FCSTD DOCUMENT  (FreeCAD 1.0R39109 (Git))
Label: L_Triangla
License: All rights reserved
LicenseURL: https://en.wikipedia.org/wiki/All_rights_reserved
objects: Sketcher::SketchObject×1, PartDesign::Body×1
note: 3 computed .brp shape members not serialized (recipe doc carries the construction recipe); baked Part::Feature solids carry a one-line shape summary decoded from their .brp

FEATURE [Sketcher::SketchObject] Sketch
  ArcFitTolerance = 1e-06
  AttachmentSupport = -> [XY_Plane]
  FullyConstrained = true
  MakeInternals = false
  MapMode = 5
  sketch-geometry (8):
    g0: LineSegment StartX=0 StartY=0 StartZ=0 EndX=45 EndY=77.9423 EndZ=0
    g1: LineSegment StartX=45 StartY=77.9423 StartZ=0 EndX=89.9999 EndY=0 EndZ=0
    g2: LineSegment StartX=89.9999 StartY=0 StartZ=0 EndX=0 EndY=0 EndZ=0
    g3: Circle CenterX=15 CenterY=10 CenterZ=0 NormalX=0 NormalY=0 NormalZ=1 AngleXU=0 Radius=2.5
    g4: Circle CenterX=45 CenterY=10 CenterZ=0 NormalX=0 NormalY=0 NormalZ=1 AngleXU=0 Radius=2.5
    g5: Circle CenterX=75 CenterY=10 CenterZ=0 NormalX=0 NormalY=0 NormalZ=1 AngleXU=0 Radius=2.5
    g6: Circle CenterX=39.5 CenterY=63 CenterZ=0 NormalX=0 NormalY=0 NormalZ=1 AngleXU=0 Radius=1.5
    g7: Circle CenterX=50.5 CenterY=63 CenterZ=0 NormalX=0 NormalY=0 NormalZ=1 AngleXU=0 Radius=1.5
  constraints (23):
    c: Distance(g0) = 90
    c: Angle(g-1,g0) = 1.0472
    c: Coincident(g0,g-1)
    c: Distance(g1) = 90
    c: Coincident(g1,g0)
    c: PointOnObject(g1,g-1)
    c: Coincident(g2,g1)
    c: Coincident(g2,g0)
    c: Diameter(g3) = 5
    c: Diameter(g4) = 5
    c: Diameter(g5) = 5
    c: DistanceY(g4,g3) = 0
    c: DistanceY(g4,g5) = 0
    c: DistanceX(g0,g4) = 45
    c: DistanceX(g3,g4) = 30
    c: DistanceX(g4,g5) = 30
    c: DistanceY(g0,g4) = 10
    c: Diameter(g6) = 3
    c: Diameter(g7) = 3
    c: DistanceY(g7,g6) = 0
    c: DistanceY(g4,g7) = 53
    c: DistanceX(g6,g7) = 11
    c: DistanceX(g6,g0) = 5.5
FEATURE [PartDesign::Body] Body
  AllowCompound = false
  Group = -> [Sketch]
  Origin = -> Origin
